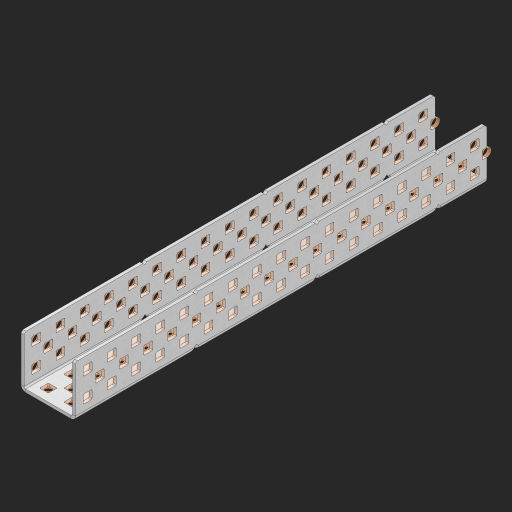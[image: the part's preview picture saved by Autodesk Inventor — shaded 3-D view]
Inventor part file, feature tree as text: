
AUTODESK INVENTOR PART (.ipt)
format: ipt  version: 2023 (Build 270158000, 158)  size: 2,011,648 bytes
history: native  units: in
note: dims shown in document units (in); Inventor stores cm internally (conversion verified against a paired STEP export)
features: other x210, extrude x202, sheet_metal_op x8, sketch x7, mirror x3, pattern_linear x2, chamfer x1
ambient origin geometry x8: Origin, YZ Plane, XZ Plane, XY Plane, X Axis, Y Axis, Z Axis, Center Point
bodies: Solid1 (feature_tree), Body (feature_tree)
feature tree (433):
  sheet_metal_op  "Flanges"
  sheet_metal_op  "Body Pattern"
  pattern_linear  "Center Pattern"  Spacing1=1.0in  [1 undecoded]
  other  "Arc Length"
  mirror  "Notch Mirror"
  pattern_linear  "Notch Pattern"  Spacing1=0.25in  [1 undecoded]
  other  "Diagonal Plane"
  mirror  "Flange 1"
  mirror  "Flange 2"
  chamfer  "End Chamfer"
  sketch  "Sketch1"  dims[d0=1.0in]
  other  "Plate1"
  sketch  "Sketch2"  dims[d1=8.5in]
  other  "Plate2"
  sheet_metal_op  "Bend1"
  sheet_metal_op  "Corner1"
  sketch  "Sketch8"  dims[d2=0.0625in]
  sketch  "Sketch9"  dims[d3=0.0625in]
  other  "Srf91"
  sheet_metal_op  "Body Pattern Sketch"
  other  "Srf92"
  sketch  "Sketch13"  dims[d4=0.0312in]
  sketch  "Sketch15"  dims[d5=0.125in]
  sketch  "Sketch16"  dims[d6=0.0625in d7=1.0in d8=90.0deg d9=0.0312in d10=0.25in d11=0.0625in d12=0.0625in d49=0.182in d50=0.02in d52=0.25in d53=0.0625in d54=0.0in d55=0.172in d56=1.0in d57=0.0in d60=6.6929in d62=0.5in d63=0.7874in d65=0.5in d85=0.1473in d86=0.1782in d88=0.04in d89=0.0625in d90=0.0in d91=0.04in d92=0.0491in d95=2.5in d96=0.04in d97=0.25in d98=45.0deg d99=0.25in d102=2.497in d106=0.182in d107=0.02in d108=0.5in d110=0.0625in d111=0.0in d112=0.172in d113=0.5in d114=0.0in d117=0.5in d118=0.5in d131=0.25in d132=0.25in]
  other  "Srf786"
  other  "Srf889"
  other  "Srf890"
  other  "Srf891"
  other  "Srf892"
  other  "Srf893"
  other  "Srf894"
  other  "Srf895"
  other  "Srf896"
  other  "Srf996"
  other  "Srf997"
  other  "Srf998"
  other  "Srf999"
  other  "Srf1000"
  other  "Srf1255"
  other  "Srf1256"
  other  "Srf1257"
  other  "Srf1315"
  other  "Srf1316"
  other  "Srf1317"
  other  "Srf1325"
  other  "Srf1326"
  other  "Srf1327"
  other  "Srf1328"
  other  "Srf1329"
  other  "Srf1330"
  other  "Srf1331"
  other  "Srf1332"
  other  "Srf1338"
  other  "Srf1339"
  other  "Srf1340"
  other  "Srf1341"
  other  "Srf1342"
  other  "Srf1369"
  other  "Srf1370"
  other  "Srf1371"
  other  "Srf1374"
  other  "Srf1375"
  other  "Srf1376"
  other  "Srf1384"
  other  "Srf1385"
  other  "Srf1386"
  other  "Srf1387"
  other  "Srf1388"
  other  "Srf1389"
  other  "Srf1390"
  other  "Srf1391"
  other  "Srf1397"
  other  "Srf1398"
  other  "Srf1399"
  other  "Srf1400"
  other  "Srf1401"
  other  "Srf1428"
  other  "Srf1429"
  other  "Srf1430"
  other  "Srf1433"
  other  "Srf1434"
  other  "Srf1473"
  other  "Srf1474"
  other  "Srf1475"
  other  "Srf1476"
  other  "Srf1477"
  other  "Srf1478"
  other  "Srf1479"
  other  "Srf1480"
  other  "Srf1481"
  other  "Srf1482"
  other  "Srf1483"
  other  "Srf1484"
  other  "Srf1485"
  other  "Srf1486"
  other  "Srf1487"
  other  "Srf1488"
  other  "Srf1489"
  other  "Srf1500"
  other  "Srf1501"
  other  "Srf1502"
  other  "Srf1503"
  other  "Srf1504"
  other  "Srf1505"
  other  "Srf1506"
  other  "Srf1507"
  other  "Srf1508"
  other  "Srf1509"
  other  "Srf1510"
  other  "Srf1511"
  other  "Srf1512"
  other  "Srf1513"
  other  "Srf1514"
  other  "Srf1515"
  other  "Srf1516"
  other  "Srf1517"
  other  "Srf1518"
  other  "Srf1519"
  other  "Srf1520"
  other  "Srf1521"
  other  "Srf1522"
  other  "Srf1523"
  other  "Srf1524"
  other  "Srf1525"
  other  "Srf1526"
  other  "Srf1527"
  other  "Srf1528"
  other  "Srf1529"
  other  "Srf1530"
  other  "Srf1531"
  other  "Srf1538"
  other  "Srf1539"
  other  "Srf1540"
  other  "Srf1541"
  other  "Srf1542"
  other  "Srf1543"
  other  "Srf1544"
  other  "Srf1545"
  other  "Srf1546"
  other  "Srf1547"
  other  "Srf1548"
  other  "Srf1549"
  other  "Srf1550"
  other  "Srf1551"
  other  "Srf1552"
  other  "Srf1553"
  other  "Srf1554"
  other  "Srf1555"
  other  "Srf1556"
  other  "Srf1557"
  other  "Srf1558"
  other  "Srf1559"
  other  "Srf1560"
  other  "Srf1561"
  other  "Srf1562"
  other  "Srf1563"
  other  "Srf1564"
  other  "Srf1565"
  other  "Srf1566"
  other  "Srf1567"
  other  "Srf1568"
  other  "Srf1569"
  other  "Srf1576"
  other  "Srf1577"
  other  "Srf1578"
  other  "Srf1579"
  other  "Srf1580"
  other  "Srf1581"
  other  "Srf1582"
  other  "Srf1583"
  other  "Srf1584"
  other  "Srf1585"
  other  "Srf1586"
  other  "Srf1587"
  other  "Srf1588"
  other  "Srf1589"
  other  "Srf1590"
  other  "Srf1591"
  other  "Srf1592"
  other  "Srf1593"
  other  "Srf1594"
  other  "Srf1595"
  other  "Srf1596"
  other  "Srf1597"
  other  "Srf1598"
  other  "Srf1599"
  other  "Srf1600"
  other  "Srf1601"
  other  "Srf1602"
  other  "Srf1603"
  other  "Srf1604"
  other  "Srf1605"
  other  "Srf1606"
  other  "Srf1607"
  other  "Srf1614"
  other  "Srf1615"
  other  "Srf1616"
  other  "Srf1617"
  other  "Srf1618"
  other  "Srf1619"
  other  "Srf1620"
  other  "Srf1621"
  other  "Srf1622"
  other  "Srf1623"
  other  "Srf1624"
  other  "Srf1625"
  other  "Srf1626"
  other  "Srf1627"
  other  "Srf1628"
  other  "Srf1629"
  other  "Srf1630"
  other  "Srf1631"
  other  "Srf1632"
  other  "Srf1633"
  other  "Srf1634"
  other  "Srf1635"
  other  "Srf1636"
  other  "Srf1637"
  other  "Srf1638"
  other  "Srf1639"
  other  "Srf1640"
  other  "Srf1641"
  other  "Srf1642"
  other  "Srf1643"
  other  "Srf1644"
  other  "Srf1645"
  sheet_metal_op  "Body Stamp"
  sheet_metal_op  "Body Circle"
  other  "Center Stamp"
  other  "Center Circle"
  sheet_metal_op  "Notch"
  extrude  "ExtrusionSrf92"  Depth=0.0625in
  extrude  "ExtrusionSrf889"  Depth=0.0625in
  extrude  "ExtrusionSrf890"  Depth=0.182in
  extrude  "ExtrusionSrf891"  Depth=0.02in
  extrude  "ExtrusionSrf892"  Depth=0.25in
  extrude  "ExtrusionSrf893"  Depth=0.0625in
  extrude  "ExtrusionSrf894"  TaperAngle=0.0deg  [1 undecoded]
  extrude  "ExtrusionSrf895"  Depth=0.25in
  extrude  "ExtrusionSrf896"  Depth=1.0in TaperAngle=0.0deg
  extrude  "ExtrusionSrf996"  Depth=0.25in
  extrude  "ExtrusionSrf997"  Depth=0.5in
  extrude  "ExtrusionSrf998"  Depth=0.25in
  extrude  "ExtrusionSrf999"  Depth=0.25in
  extrude  "ExtrusionSrf1000"  Depth=0.25in
  extrude  "ExtrusionSrf1255"  Depth=0.0625in
  extrude  "ExtrusionSrf1256"  TaperAngle=0.0deg  [1 undecoded]
  extrude  "ExtrusionSrf1257"  Depth=0.25in
  extrude  "ExtrusionSrf1315"  Depth=0.25in
  extrude  "ExtrusionSrf1316"  Depth=2.5in
  extrude  "ExtrusionSrf1355"  Depth=0.25in TaperAngle=45.0deg
  extrude  "ExtrusionSrf1356"  Depth=0.25in
  extrude  "ExtrusionSrf1357"  Depth=0.25in
  extrude  "ExtrusionSrf1358"  Depth=0.182in
  extrude  "ExtrusionSrf1359"  Depth=0.02in
  extrude  "ExtrusionSrf1360"  Depth=0.5in
  extrude  "ExtrusionSrf1361"  Depth=0.0625in
  extrude  "ExtrusionSrf1362"  TaperAngle=0.0deg  [1 undecoded]
  extrude  "ExtrusionSrf1363"  Depth=0.25in
  extrude  "ExtrusionSrf1364"  Depth=0.5in TaperAngle=0.0deg
  extrude  "ExtrusionSrf1365"  Depth=0.5in
  extrude  "ExtrusionSrf1366"  Depth=0.5in
  extrude  "ExtrusionSrf1367"  Depth=0.25in
  extrude  "ExtrusionSrf1368"  Depth=0.25in
  extrude  "ExtrusionSrf1369"  [1 undecoded]
  extrude  "ExtrusionSrf1370"  [1 undecoded]
  extrude  "ExtrusionSrf1371"  [1 undecoded]
  extrude  "ExtrusionSrf1374"  [1 undecoded]
  extrude  "ExtrusionSrf1375"  [1 undecoded]
  extrude  "ExtrusionSrf1414"  [1 undecoded]
  extrude  "ExtrusionSrf1415"  [1 undecoded]
  extrude  "ExtrusionSrf1416"  [1 undecoded]
  extrude  "ExtrusionSrf1417"  [1 undecoded]
  extrude  "ExtrusionSrf1418"  [1 undecoded]
  extrude  "ExtrusionSrf1419"  [1 undecoded]
  extrude  "ExtrusionSrf1420"  [1 undecoded]
  extrude  "ExtrusionSrf1421"  [1 undecoded]
  extrude  "ExtrusionSrf1422"  [1 undecoded]
  extrude  "ExtrusionSrf1423"  [1 undecoded]
  extrude  "ExtrusionSrf1424"  [1 undecoded]
  extrude  "ExtrusionSrf1425"  [1 undecoded]
  extrude  "ExtrusionSrf1426"  [1 undecoded]
  extrude  "ExtrusionSrf1427"  [1 undecoded]
  extrude  "ExtrusionSrf1428"  [1 undecoded]
  extrude  "ExtrusionSrf1429"  [1 undecoded]
  extrude  "ExtrusionSrf1430"  [1 undecoded]
  extrude  "ExtrusionSrf1433"  [1 undecoded]
  extrude  "ExtrusionSrf1434"  [1 undecoded]
  extrude  "ExtrusionSrf1473"  [1 undecoded]
  extrude  "ExtrusionSrf1474"  [1 undecoded]
  extrude  "ExtrusionSrf1475"  [1 undecoded]
  extrude  "ExtrusionSrf1476"  [1 undecoded]
  extrude  "ExtrusionSrf1477"  [1 undecoded]
  extrude  "ExtrusionSrf1478"  [1 undecoded]
  extrude  "ExtrusionSrf1479"  [1 undecoded]
  extrude  "ExtrusionSrf1480"  [1 undecoded]
  extrude  "ExtrusionSrf1481"  [1 undecoded]
  extrude  "ExtrusionSrf1482"  [1 undecoded]
  extrude  "ExtrusionSrf1483"  [1 undecoded]
  extrude  "ExtrusionSrf1484"  [1 undecoded]
  extrude  "ExtrusionSrf1485"  [1 undecoded]
  extrude  "ExtrusionSrf1486"  [1 undecoded]
  extrude  "ExtrusionSrf1487"  [1 undecoded]
  extrude  "ExtrusionSrf1488"  [1 undecoded]
  extrude  "ExtrusionSrf1489"  [1 undecoded]
  extrude  "ExtrusionSrf1500"  [1 undecoded]
  extrude  "ExtrusionSrf1501"  [1 undecoded]
  extrude  "ExtrusionSrf1502"  [1 undecoded]
  extrude  "ExtrusionSrf1503"  [1 undecoded]
  extrude  "ExtrusionSrf1504"  [1 undecoded]
  extrude  "ExtrusionSrf1505"  [1 undecoded]
  extrude  "ExtrusionSrf1506"  [1 undecoded]
  extrude  "ExtrusionSrf1507"  [1 undecoded]
  extrude  "ExtrusionSrf1508"  [1 undecoded]
  extrude  "ExtrusionSrf1509"  [1 undecoded]
  extrude  "ExtrusionSrf1510"  [1 undecoded]
  extrude  "ExtrusionSrf1511"  [1 undecoded]
  extrude  "ExtrusionSrf1512"  [1 undecoded]
  extrude  "ExtrusionSrf1513"  [1 undecoded]
  extrude  "ExtrusionSrf1514"  [1 undecoded]
  extrude  "ExtrusionSrf1515"  [1 undecoded]
  extrude  "ExtrusionSrf1516"  [1 undecoded]
  extrude  "ExtrusionSrf1517"  [1 undecoded]
  extrude  "ExtrusionSrf1518"  [1 undecoded]
  extrude  "ExtrusionSrf1519"  [1 undecoded]
  extrude  "ExtrusionSrf1520"  [1 undecoded]
  extrude  "ExtrusionSrf1521"  [1 undecoded]
  extrude  "ExtrusionSrf1522"  [1 undecoded]
  extrude  "ExtrusionSrf1523"  [1 undecoded]
  extrude  "ExtrusionSrf1524"  [1 undecoded]
  extrude  "ExtrusionSrf1525"  [1 undecoded]
  extrude  "ExtrusionSrf1526"  [1 undecoded]
  extrude  "ExtrusionSrf1527"  [1 undecoded]
  extrude  "ExtrusionSrf1528"  [1 undecoded]
  extrude  "ExtrusionSrf1529"  [1 undecoded]
  extrude  "ExtrusionSrf1530"  [1 undecoded]
  extrude  "ExtrusionSrf1531"  [1 undecoded]
  extrude  "ExtrusionSrf1538"  [1 undecoded]
  extrude  "ExtrusionSrf1539"  [1 undecoded]
  extrude  "ExtrusionSrf1540"  [1 undecoded]
  extrude  "ExtrusionSrf1541"  [1 undecoded]
  extrude  "ExtrusionSrf1542"  [1 undecoded]
  extrude  "ExtrusionSrf1543"  [1 undecoded]
  extrude  "ExtrusionSrf1544"  [1 undecoded]
  extrude  "ExtrusionSrf1545"  [1 undecoded]
  extrude  "ExtrusionSrf1546"  [1 undecoded]
  extrude  "ExtrusionSrf1547"  [1 undecoded]
  extrude  "ExtrusionSrf1548"  [1 undecoded]
  extrude  "ExtrusionSrf1549"  [1 undecoded]
  extrude  "ExtrusionSrf1550"  [1 undecoded]
  extrude  "ExtrusionSrf1551"  [1 undecoded]
  extrude  "ExtrusionSrf1552"  [1 undecoded]
  extrude  "ExtrusionSrf1553"  [1 undecoded]
  extrude  "ExtrusionSrf1554"  [1 undecoded]
  extrude  "ExtrusionSrf1555"  [1 undecoded]
  extrude  "ExtrusionSrf1556"  [1 undecoded]
  extrude  "ExtrusionSrf1557"  [1 undecoded]
  extrude  "ExtrusionSrf1558"  [1 undecoded]
  extrude  "ExtrusionSrf1559"  [1 undecoded]
  extrude  "ExtrusionSrf1560"  [1 undecoded]
  extrude  "ExtrusionSrf1561"  [1 undecoded]
  extrude  "ExtrusionSrf1562"  [1 undecoded]
  extrude  "ExtrusionSrf1563"  [1 undecoded]
  extrude  "ExtrusionSrf1564"  [1 undecoded]
  extrude  "ExtrusionSrf1565"  [1 undecoded]
  extrude  "ExtrusionSrf1566"  [1 undecoded]
  extrude  "ExtrusionSrf1567"  [1 undecoded]
  extrude  "ExtrusionSrf1568"  [1 undecoded]
  extrude  "ExtrusionSrf1569"  [1 undecoded]
  extrude  "ExtrusionSrf1576"  [1 undecoded]
  extrude  "ExtrusionSrf1577"  [1 undecoded]
  extrude  "ExtrusionSrf1578"  [1 undecoded]
  extrude  "ExtrusionSrf1579"  [1 undecoded]
  extrude  "ExtrusionSrf1580"  [1 undecoded]
  extrude  "ExtrusionSrf1581"  [1 undecoded]
  extrude  "ExtrusionSrf1582"  [1 undecoded]
  extrude  "ExtrusionSrf1583"  [1 undecoded]
  extrude  "ExtrusionSrf1584"  [1 undecoded]
  extrude  "ExtrusionSrf1585"  [1 undecoded]
  extrude  "ExtrusionSrf1586"  [1 undecoded]
  extrude  "ExtrusionSrf1587"  [1 undecoded]
  extrude  "ExtrusionSrf1588"  [1 undecoded]
  extrude  "ExtrusionSrf1589"  [1 undecoded]
  extrude  "ExtrusionSrf1590"  [1 undecoded]
  extrude  "ExtrusionSrf1591"  [1 undecoded]
  extrude  "ExtrusionSrf1592"  [1 undecoded]
  extrude  "ExtrusionSrf1593"  [1 undecoded]
  extrude  "ExtrusionSrf1594"  [1 undecoded]
  extrude  "ExtrusionSrf1595"  [1 undecoded]
  extrude  "ExtrusionSrf1596"  [1 undecoded]
  extrude  "ExtrusionSrf1597"  [1 undecoded]
  extrude  "ExtrusionSrf1598"  [1 undecoded]
  extrude  "ExtrusionSrf1599"  [1 undecoded]
  extrude  "ExtrusionSrf1600"  [1 undecoded]
  extrude  "ExtrusionSrf1601"  [1 undecoded]
  extrude  "ExtrusionSrf1602"  [1 undecoded]
  extrude  "ExtrusionSrf1603"  [1 undecoded]
  extrude  "ExtrusionSrf1604"  [1 undecoded]
  extrude  "ExtrusionSrf1605"  [1 undecoded]
  extrude  "ExtrusionSrf1606"  [1 undecoded]
  extrude  "ExtrusionSrf1607"  [1 undecoded]
  extrude  "ExtrusionSrf1614"  [1 undecoded]
  extrude  "ExtrusionSrf1615"  [1 undecoded]
  extrude  "ExtrusionSrf1616"  [1 undecoded]
  extrude  "ExtrusionSrf1617"  [1 undecoded]
  extrude  "ExtrusionSrf1618"  [1 undecoded]
  extrude  "ExtrusionSrf1619"  [1 undecoded]
  extrude  "ExtrusionSrf1620"  [1 undecoded]
  extrude  "ExtrusionSrf1621"  [1 undecoded]
  extrude  "ExtrusionSrf1622"  [1 undecoded]
  extrude  "ExtrusionSrf1623"  [1 undecoded]
  extrude  "ExtrusionSrf1624"  [1 undecoded]
  extrude  "ExtrusionSrf1625"  [1 undecoded]
  extrude  "ExtrusionSrf1626"  [1 undecoded]
  extrude  "ExtrusionSrf1627"  [1 undecoded]
  extrude  "ExtrusionSrf1628"  [1 undecoded]
  extrude  "ExtrusionSrf1629"  [1 undecoded]
  extrude  "ExtrusionSrf1630"  [1 undecoded]
  extrude  "ExtrusionSrf1631"  [1 undecoded]
  extrude  "ExtrusionSrf1632"  [1 undecoded]
  extrude  "ExtrusionSrf1633"  [1 undecoded]
  extrude  "ExtrusionSrf1634"  [1 undecoded]
  extrude  "ExtrusionSrf1635"  [1 undecoded]
  extrude  "ExtrusionSrf1636"  [1 undecoded]
  extrude  "ExtrusionSrf1637"  [1 undecoded]
  extrude  "ExtrusionSrf1638"  [1 undecoded]
  extrude  "ExtrusionSrf1639"  [1 undecoded]
  extrude  "ExtrusionSrf1640"  [1 undecoded]
  extrude  "ExtrusionSrf1641"  [1 undecoded]
  extrude  "ExtrusionSrf1642"  [1 undecoded]
  extrude  "ExtrusionSrf1643"  [1 undecoded]
  extrude  "ExtrusionSrf1644"  [1 undecoded]
  extrude  "ExtrusionSrf1645"  [1 undecoded]
note: 174 required parameter values undecoded (feature->parameter linkage not recoverable at this tier; creation-order binding heuristic only, values carry confidence <= 0.55)
